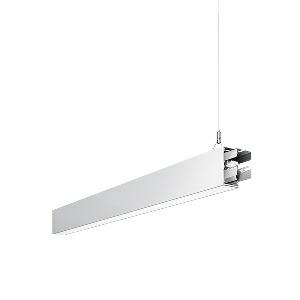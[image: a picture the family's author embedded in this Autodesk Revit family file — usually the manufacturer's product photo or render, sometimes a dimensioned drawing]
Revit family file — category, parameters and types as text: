
# Revit family: idoo_line_-_ilp_4000_830_d_mid_00805737_f616
name_source: partatom
category: Lighting Fixtures
units: mm (PartAtom-declared; Revit-internal decimal feet)

## family parameters
Cut with Voids When Loaded = No
Host = Face
Light Source = No
Part Type = Normal
Room Calculation Point = No
Round Connector Dimension = Use Diameter
Shared = No

## types (1)
- IDOO.line - ILP 4000/830/D MID (1 x LED, 3750 lm, 3000K)
    Apparent Load = 29 VA
    Approval mark = CE
    CIE Flux Codes = 66 91 98 40 100
    Color Rendering = 80-89
    Color Temperature = 3000K
    Control Gear = Electronic ballast
    Default Elevation = 1800 mm
    Description = ILP 4000/830/D|Suspended luminaire|light source: LED|connected load: 220-240 V, 50/60 Hz|Power consumption: approx. 29 W|standby: approx. 0,15|luminous flux: 3750 lm|luminous efficacy: 129 lm/W|light distribution: Direct/indirect|direct ratio: approx. 40 %|colour temperature: Warm white, ca. 3000 K|color rendering index (CRI): >= 80|chromaticity tolerance:  3 SDCM|System of protection: IP 40|technology: Continuously dimmable|luminaire body|material: Sectional aluminium|colour: White|lamp cover: Acrylic (PMMA), Clear|mains lead: 1,0 m With free stranded wires|Fastening: Steel cable 0.3 - 0.7 m|glare control: Prism aperture|luminance(L65): <= 2700 cd/m|unified glare rating(4H 8H): <=  16|special features: DALI Load 1x, TouchDIM - dimming via standard switch, Through-wired, up to 18 m on one mains connection, Flicker-free, Suitable as emergency lighting, Mechanical and electrical connection of the individual modules without tools|
    Frequency = 50 Hz
    Height = 110 mm
    Lamp = 1 x LED
    Lamp Light Flux = 3750 lm
    Lamp count = 1
    Length = 1402 mm
    Luminous efficacy = 129 lm/W
    Manufacturer = Waldmann
    ModVariant = No
    Model = 00805737
    Mounting Place = Ceiling
    Mounting Type = Pendant
    Number of Poles = 1
    OnlyDefault = Yes
    Power Factor = 1
    Product Name = IDOO.line - ILP 4000/830/D MID
    Product group = Suspended luminaire
    ProductGroupID = 9
    Protection Class = Protection class I
    Protection Degree = IP 40
    RLX_Detail_Level = 1
    RLX_Emergency_Light_Flux = 0 lm
    RLX_Emergency_Type = 0
    RLX_Emergency_Type_DB = No
    RlxData = <blob elided: 20317 chars, md5=ebc6c50a>
    Socket = socket
    Standby Power = 0 W
    System Light Flux = 3750 lm
    System Power = 29 W
    Type Comments = Product without accessories
    Type Image = 113308000-00692588.jpg
    URL = http://relux.com
    VarID = ---
    Voltage = 230 V
    Voltage Range = 220-240 V
    Weight = 0.00 kg
    Width = 60 mm  [stored 0.19685 ft]

note: [stored X ft] marks values corroborated as IEEE doubles in the binary element streams (Revit-internal decimal feet)

## geometry (parser evidence)
native form markers: Blend x4, Sweep x13
no freeform markers — native parametric forms only
